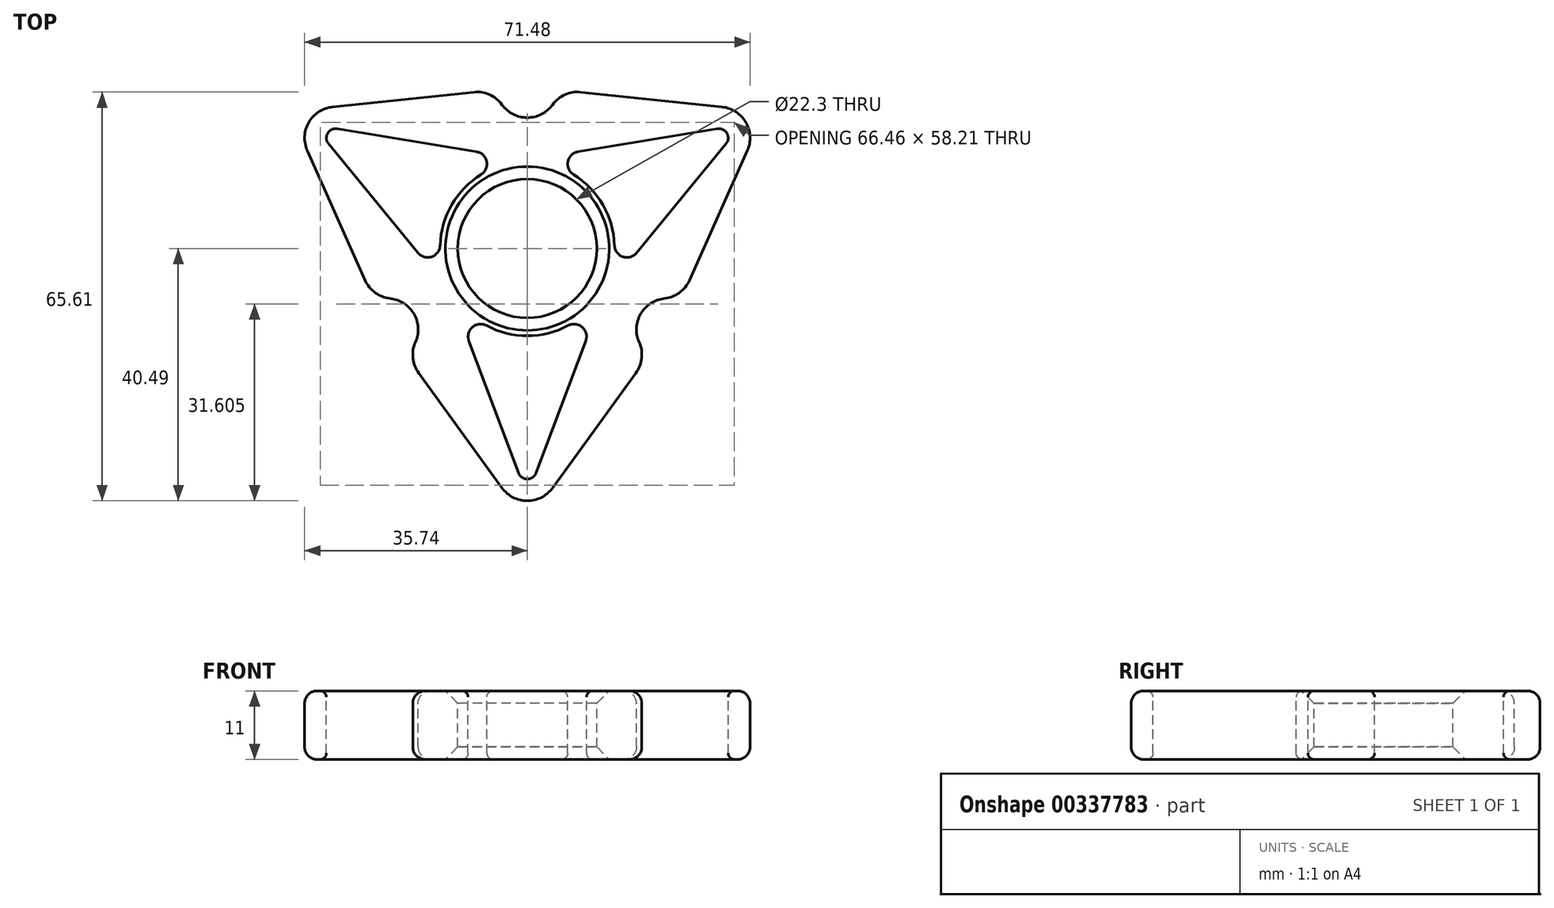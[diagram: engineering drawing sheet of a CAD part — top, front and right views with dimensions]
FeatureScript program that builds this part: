
annotation { "Feature Type Name" : "Feature", "Feature Type Description" : "" }
export const myFeature = defineFeature(function(context is Context, id is Id, definition is map)
    precondition{}
    {
        {
            var Q0;
            Q0=qCreatedBy(makeId("Top.planeOp"),FACE);
            var sketch = newSketch(context, id + "F0", { "sketchPlane" : qUnion([Q0])});
            skCircle(sketch, "E0.cCircle", {"center": v(0, 0) * mm, "radius": 22 * mm, "construction": true});
            skLineSegment(sketch, "E0.0", {"start": v(-38.1, 22) * mm, "end": v(38.1, 22) * mm});
            skLineSegment(sketch, "E0.1", {"start": v(38.1, 22) * mm, "end": v(0, -44) * mm});
            skLineSegment(sketch, "E0.2", {"start": v(0, -44) * mm, "end": v(-38.1, 22) * mm});
            skPoint(sketch, "E0.0.midPoint", {"position": v(0, 22) * mm});
            skLineSegment(sketch, "E1", {"start": v(-38.1, 22) * mm, "end": v(0, 26) * mm});
            skLineSegment(sketch, "E2", {"start": v(0, 26) * mm, "end": v(38.1, 22) * mm});
            skLineSegment(sketch, "E3.1.0", {"start": v(0, -44) * mm, "end": v(-22.52, -13) * mm});
            skLineSegment(sketch, "E3.1.1", {"start": v(-22.52, -13) * mm, "end": v(-38.1, 22) * mm});
            skLineSegment(sketch, "E3.2.0", {"start": v(38.1, 22) * mm, "end": v(22.52, -13) * mm});
            skLineSegment(sketch, "E3.2.1", {"start": v(22.52, -13) * mm, "end": v(0, -44) * mm});
            skSolve(sketch);
        }
        {
            var Q0;
            Q0 = qSketchRegion(id + "F0", true);
            extrude(context, id + "F1", {"entities" : qUnion([Q0]), "depth" : 11 * mm});
        }
        {
            var Q0;
            Q0=makeQuery(id+"F1.opExtrude","CAP_FACE",FACE,{"disambiguationData":[OSD([sQuery(id+"F0.wireOp",EDGE,"E1"),sQuery(id+"F0.wireOp",EDGE,"E2"),sQuery(id+"F0.wireOp",EDGE,"E3.1.0"),sQuery(id+"F0.wireOp",EDGE,"E3.1.1"),sQuery(id+"F0.wireOp",EDGE,"E3.2.0"),sQuery(id+"F0.wireOp",EDGE,"E3.2.1")])],"isStart":false});
            var sketch = newSketch(context, id + "F2", { "sketchPlane" : qUnion([Q0])});
            skCircle(sketch, "E4", {"center": v(0, 0) * mm, "radius": 11.15 * mm});
            skSolve(sketch);
        }
        {
            var Q0;
            Q0 = qSketchRegion(id + "F2", true);
            extrude(context, id + "F3", {"entities" : qUnion([Q0]), "operationType" : NewBodyOperationType.REMOVE, "endBound" : BoundingType.THROUGH_ALL, "oppositeDirection" : true, "depth" : 25 * mm});
        }
        {
            var Q0;
            Q0=makeQuery(id+"F1.opExtrude","SWEPT_EDGE",EDGE,{"disambiguationData":[OSD([sQuery(id+"F0.wireOp",EDGE,"E0.1"),sQuery(id+"F0.wireOp",EDGE,"E0.2"),sQuery(id+"F0.wireOp",EDGE,"E3.1.0"),sQuery(id+"F0.wireOp",EDGE,"E3.2.1")])]});
            var Q1;
            Q1=makeQuery(id+"F1.opExtrude","SWEPT_EDGE",EDGE,{"disambiguationData":[OSD([sQuery(id+"F0.wireOp",EDGE,"E0.0"),sQuery(id+"F0.wireOp",EDGE,"E0.2"),sQuery(id+"F0.wireOp",EDGE,"E1"),sQuery(id+"F0.wireOp",EDGE,"E3.1.1")])]});
            var Q2;
            Q2=makeQuery(id+"F1.opExtrude","SWEPT_EDGE",EDGE,{"disambiguationData":[OSD([sQuery(id+"F0.wireOp",EDGE,"E0.0"),sQuery(id+"F0.wireOp",EDGE,"E0.1"),sQuery(id+"F0.wireOp",EDGE,"E2"),sQuery(id+"F0.wireOp",EDGE,"E3.2.0")])]});
            fillet(context, id + "F4", {"entities" : qUnion([Q0, Q1, Q2]), "radius" : 5 * mm, "tangentPropagation" : true, "allowEdgeOverflow" : false});
        }
        {
            var Q0;
            Q0=makeQuery(id+"F1.opExtrude","CAP_FACE",FACE,{"disambiguationData":[OSD([sQuery(id+"F0.wireOp",EDGE,"E1"),sQuery(id+"F0.wireOp",EDGE,"E2"),sQuery(id+"F0.wireOp",EDGE,"E3.1.0"),sQuery(id+"F0.wireOp",EDGE,"E3.1.1"),sQuery(id+"F0.wireOp",EDGE,"E3.2.0"),sQuery(id+"F0.wireOp",EDGE,"E3.2.1")])],"isStart":false});
            var sketch = newSketch(context, id + "F5", { "sketchPlane" : qUnion([Q0])});
            skArc(sketch, "E5", {"start": v(-4.05, 23.06) * mm, "mid": v(0, 21) * mm, "end": v(4.05, 23.06) * mm});
            skLineSegment(sketch, "E6", {"start": v(-31.26, 22.72) * mm, "end": v(-8.61, 25.1) * mm});
            skLineSegment(sketch, "E7", {"start": v(8.61, 25.1) * mm, "end": v(31.26, 22.72) * mm});
            skPoint(sketch, "E8.visualSharp", {"position": v(-4.97, 25.48) * mm});
            skArc(sketch, "E8.filletArc", {"start": v(-4.05, 23.06) * mm, "mid": v(-6.06, 24.7) * mm, "end": v(-8.61, 25.1) * mm});
            skPoint(sketch, "E9.visualSharp", {"position": v(4.97, 25.48) * mm});
            skArc(sketch, "E9.filletArc", {"start": v(8.61, 25.1) * mm, "mid": v(6.06, 24.7) * mm, "end": v(4.05, 23.06) * mm});
            skLineSegment(sketch, "E10", {"start": v(-8.61, 25.1) * mm, "end": v(0, 26) * mm});
            skLineSegment(sketch, "E11", {"start": v(8.61, 25.1) * mm, "end": v(0, 26) * mm});
            skLineSegment(sketch, "E12.1.0", {"start": v(-4.05, -38.43) * mm, "end": v(-17.43, -20) * mm});
            skLineSegment(sketch, "E12.1.1", {"start": v(-26.04, -5.09) * mm, "end": v(-35.3, 15.71) * mm});
            skPoint(sketch, "E12.1.2", {"position": v(-24.55, -8.43) * mm});
            skLineSegment(sketch, "E12.1.3", {"start": v(-17.43, -20) * mm, "end": v(-22.52, -13) * mm});
            skLineSegment(sketch, "E12.1.4", {"start": v(-26.04, -5.09) * mm, "end": v(-22.52, -13) * mm});
            skPoint(sketch, "E12.1.5", {"position": v(-19.58, -17.05) * mm});
            skArc(sketch, "E12.1.6", {"start": v(-17.95, -15.03) * mm, "mid": v(-18.19, -10.5) * mm, "end": v(-22, -8.03) * mm});
            skArc(sketch, "E12.1.7", {"start": v(-17.95, -15.03) * mm, "mid": v(-18.35, -17.6) * mm, "end": v(-17.43, -20) * mm});
            skArc(sketch, "E12.1.8", {"start": v(-26.04, -5.09) * mm, "mid": v(-24.41, -7.1) * mm, "end": v(-22, -8.03) * mm});
            skLineSegment(sketch, "E12.2.0", {"start": v(35.3, 15.71) * mm, "end": v(26.04, -5.09) * mm});
            skLineSegment(sketch, "E12.2.1", {"start": v(17.43, -20) * mm, "end": v(4.05, -38.43) * mm});
            skPoint(sketch, "E12.2.2", {"position": v(19.58, -17.05) * mm});
            skLineSegment(sketch, "E12.2.3", {"start": v(26.04, -5.09) * mm, "end": v(22.52, -13) * mm});
            skLineSegment(sketch, "E12.2.4", {"start": v(17.43, -20) * mm, "end": v(22.52, -13) * mm});
            skPoint(sketch, "E12.2.5", {"position": v(24.55, -8.43) * mm});
            skArc(sketch, "E12.2.6", {"start": v(22, -8.03) * mm, "mid": v(18.19, -10.5) * mm, "end": v(17.95, -15.03) * mm});
            skArc(sketch, "E12.2.7", {"start": v(22, -8.03) * mm, "mid": v(24.41, -7.1) * mm, "end": v(26.04, -5.09) * mm});
            skArc(sketch, "E12.2.8", {"start": v(17.43, -20) * mm, "mid": v(18.35, -17.6) * mm, "end": v(17.95, -15.03) * mm});
            skPoint(sketch, "E12.center", {"position": v(0, 0) * mm});
            skSolve(sketch);
        }
        {
            var Q0;
            Q0 = qSketchRegion(id + "F5", true);
            extrude(context, id + "F6", {"entities" : qUnion([Q0]), "operationType" : NewBodyOperationType.REMOVE, "endBound" : BoundingType.THROUGH_ALL, "oppositeDirection" : true, "depth" : 25 * mm});
        }
        {
            var Q0;
            Q0=makeQuery(id+"F1.opExtrude","CAP_FACE",FACE,{"disambiguationData":[OSD([sQuery(id+"F0.wireOp",EDGE,"E1"),sQuery(id+"F0.wireOp",EDGE,"E2"),sQuery(id+"F0.wireOp",EDGE,"E3.1.0"),sQuery(id+"F0.wireOp",EDGE,"E3.1.1"),sQuery(id+"F0.wireOp",EDGE,"E3.2.0"),sQuery(id+"F0.wireOp",EDGE,"E3.2.1")])],"isStart":false});
            var sketch = newSketch(context, id + "F7", { "sketchPlane" : qUnion([Q0])});
            skArc(sketch, "E13", {"start": v(-1.4, -36.02) * mm, "mid": v(0, -37) * mm, "end": v(1.4, -36.02) * mm});
            skArc(sketch, "E14", {"start": v(-6.57, -12.36) * mm, "mid": v(0, -14) * mm, "end": v(6.57, -12.36) * mm});
            skLineSegment(sketch, "E15", {"start": v(-9.38, -14.84) * mm, "end": v(-1.4, -36.02) * mm});
            skLineSegment(sketch, "E16", {"start": v(9.38, -14.84) * mm, "end": v(1.4, -36.02) * mm});
            skPoint(sketch, "E17.visualSharp", {"position": v(-13.1, -4.93) * mm});
            skArc(sketch, "E17.filletArc", {"start": v(-6.57, -12.36) * mm, "mid": v(-8.82, -12.63) * mm, "end": v(-9.38, -14.84) * mm});
            skPoint(sketch, "E18.visualSharp", {"position": v(13.1, -4.93) * mm});
            skArc(sketch, "E18.filletArc", {"start": v(9.38, -14.84) * mm, "mid": v(8.82, -12.63) * mm, "end": v(6.57, -12.36) * mm});
            skArc(sketch, "E19.1.0", {"start": v(14, 0.5) * mm, "mid": v(12.12, 7) * mm, "end": v(7.43, 11.87) * mm});
            skArc(sketch, "E19.1.1", {"start": v(8.16, 15.54) * mm, "mid": v(6.53, 13.96) * mm, "end": v(7.43, 11.87) * mm});
            skPoint(sketch, "E19.1.2", {"position": v(10.82, -8.88) * mm});
            skPoint(sketch, "E19.1.3", {"position": v(-2.28, 13.81) * mm});
            skLineSegment(sketch, "E19.1.4", {"start": v(8.16, 15.54) * mm, "end": v(30.5, 19.23) * mm});
            skArc(sketch, "E19.1.5", {"start": v(14, 0.5) * mm, "mid": v(15.35, -1.33) * mm, "end": v(17.54, -0.7) * mm});
            skLineSegment(sketch, "E19.1.6", {"start": v(17.54, -0.7) * mm, "end": v(31.9, 16.8) * mm});
            skArc(sketch, "E19.1.7", {"start": v(31.9, 16.8) * mm, "mid": v(32.04, 18.5) * mm, "end": v(30.5, 19.23) * mm});
            skArc(sketch, "E19.2.0", {"start": v(-7.43, 11.87) * mm, "mid": v(-12.12, 7) * mm, "end": v(-14, 0.5) * mm});
            skArc(sketch, "E19.2.1", {"start": v(-17.54, -0.7) * mm, "mid": v(-15.35, -1.33) * mm, "end": v(-14, 0.5) * mm});
            skPoint(sketch, "E19.2.2", {"position": v(2.28, 13.81) * mm});
            skPoint(sketch, "E19.2.3", {"position": v(-10.82, -8.88) * mm});
            skLineSegment(sketch, "E19.2.4", {"start": v(-17.54, -0.7) * mm, "end": v(-31.9, 16.8) * mm});
            skArc(sketch, "E19.2.5", {"start": v(-7.43, 11.87) * mm, "mid": v(-6.53, 13.96) * mm, "end": v(-8.16, 15.54) * mm});
            skLineSegment(sketch, "E19.2.6", {"start": v(-8.16, 15.54) * mm, "end": v(-30.5, 19.23) * mm});
            skArc(sketch, "E19.2.7", {"start": v(-30.5, 19.23) * mm, "mid": v(-32.04, 18.5) * mm, "end": v(-31.9, 16.8) * mm});
            skSolve(sketch);
        }
        {
            var Q0;
            Q0=makeQuery(id+"F4.opFillet","BLEND_FACE",FACE,{"disambiguationData":[OSD([sQuery(id+"F0.wireOp",EDGE,"E0.0"),sQuery(id+"F0.wireOp",EDGE,"E0.2"),sQuery(id+"F0.wireOp",EDGE,"E1"),sQuery(id+"F0.wireOp",EDGE,"E3.1.1")])]});
            var Q1;
            Q1=makeQuery(id+"F1.opExtrude","SWEPT_FACE",FACE,{"disambiguationData":[OSD([sQuery(id+"F0.wireOp",EDGE,"E3.1.1")])]});
            var Q2;
            Q2=makeQuery(id+"F6.boolean.opBoolean","COPY",FACE,{"derivedFrom":makeQuery(id+"F6.opExtrude","SWEPT_FACE",FACE,{"disambiguationData":[OSD([sQuery(id+"F5.wireOp",EDGE,"E12.1.8")])]})});
            var Q3;
            Q3=makeQuery(id+"F6.boolean.opBoolean","COPY",FACE,{"derivedFrom":makeQuery(id+"F6.opExtrude","SWEPT_FACE",FACE,{"disambiguationData":[OSD([sQuery(id+"F5.wireOp",EDGE,"E12.1.6")])]})});
            var Q4;
            Q4=makeQuery(id+"F6.boolean.opBoolean","COPY",FACE,{"derivedFrom":makeQuery(id+"F6.opExtrude","SWEPT_FACE",FACE,{"disambiguationData":[OSD([sQuery(id+"F5.wireOp",EDGE,"E12.1.7")])]})});
            var Q5;
            Q5=makeQuery(id+"F1.opExtrude","SWEPT_FACE",FACE,{"disambiguationData":[OSD([sQuery(id+"F0.wireOp",EDGE,"E3.1.0")])]});
            var Q6;
            Q6=makeQuery(id+"F4.opFillet","BLEND_FACE",FACE,{"disambiguationData":[OSD([sQuery(id+"F0.wireOp",EDGE,"E0.1"),sQuery(id+"F0.wireOp",EDGE,"E0.2"),sQuery(id+"F0.wireOp",EDGE,"E3.1.0"),sQuery(id+"F0.wireOp",EDGE,"E3.2.1")])]});
            var Q7;
            Q7=makeQuery(id+"F1.opExtrude","SWEPT_FACE",FACE,{"disambiguationData":[OSD([sQuery(id+"F0.wireOp",EDGE,"E3.2.1")])]});
            var Q8;
            Q8=makeQuery(id+"F6.boolean.opBoolean","COPY",FACE,{"derivedFrom":makeQuery(id+"F6.opExtrude","SWEPT_FACE",FACE,{"disambiguationData":[OSD([sQuery(id+"F5.wireOp",EDGE,"E12.2.8")])]})});
            var Q9;
            Q9=makeQuery(id+"F6.boolean.opBoolean","COPY",FACE,{"derivedFrom":makeQuery(id+"F6.opExtrude","SWEPT_FACE",FACE,{"disambiguationData":[OSD([sQuery(id+"F5.wireOp",EDGE,"E12.2.6")])]})});
            var Q10;
            Q10=makeQuery(id+"F6.boolean.opBoolean","COPY",FACE,{"derivedFrom":makeQuery(id+"F6.opExtrude","SWEPT_FACE",FACE,{"disambiguationData":[OSD([sQuery(id+"F5.wireOp",EDGE,"E12.2.7")])]})});
            var Q11;
            Q11=makeQuery(id+"F1.opExtrude","SWEPT_FACE",FACE,{"disambiguationData":[OSD([sQuery(id+"F0.wireOp",EDGE,"E3.2.0")])]});
            var Q12;
            Q12=makeQuery(id+"F4.opFillet","BLEND_FACE",FACE,{"disambiguationData":[OSD([sQuery(id+"F0.wireOp",EDGE,"E0.0"),sQuery(id+"F0.wireOp",EDGE,"E0.1"),sQuery(id+"F0.wireOp",EDGE,"E2"),sQuery(id+"F0.wireOp",EDGE,"E3.2.0")])]});
            var Q13;
            Q13=makeQuery(id+"F1.opExtrude","SWEPT_FACE",FACE,{"disambiguationData":[OSD([sQuery(id+"F0.wireOp",EDGE,"E2")])]});
            var Q14;
            Q14=makeQuery(id+"F6.boolean.opBoolean","COPY",FACE,{"derivedFrom":makeQuery(id+"F6.opExtrude","SWEPT_FACE",FACE,{"disambiguationData":[OSD([sQuery(id+"F5.wireOp",EDGE,"E9.filletArc")])]})});
            var Q15;
            Q15=makeQuery(id+"F6.boolean.opBoolean","COPY",FACE,{"derivedFrom":makeQuery(id+"F6.opExtrude","SWEPT_FACE",FACE,{"disambiguationData":[OSD([sQuery(id+"F5.wireOp",EDGE,"E5")])]})});
            var Q16;
            Q16=makeQuery(id+"F6.boolean.opBoolean","COPY",FACE,{"derivedFrom":makeQuery(id+"F6.opExtrude","SWEPT_FACE",FACE,{"disambiguationData":[OSD([sQuery(id+"F5.wireOp",EDGE,"E8.filletArc")])]})});
            var Q17;
            Q17=makeQuery(id+"F1.opExtrude","SWEPT_FACE",FACE,{"disambiguationData":[OSD([sQuery(id+"F0.wireOp",EDGE,"E1")])]});
            fillet(context, id + "F8", {"entities" : qUnion([Q0, Q1, Q2, Q3, Q4, Q5, Q6, Q7, Q8, Q9, Q10, Q11, Q12, Q13, Q14, Q15, Q16, Q17]), "radius" : 2 * mm, "tangentPropagation" : true, "allowEdgeOverflow" : false});
        }
        {
            var Q0;
            Q0 = qSketchRegion(id + "F7", true);
            extrude(context, id + "F9", {"entities" : qUnion([Q0]), "operationType" : NewBodyOperationType.REMOVE, "endBound" : BoundingType.THROUGH_ALL, "oppositeDirection" : true, "depth" : 25 * mm});
        }
        {
            var Q0;
            Q0=makeQuery(id+"F9.boolean.opBoolean","COPY",FACE,{"derivedFrom":makeQuery(id+"F9.opExtrude","SWEPT_FACE",FACE,{"disambiguationData":[OSD([sQuery(id+"F7.wireOp",EDGE,"E19.1.7")])]})});
            var Q1;
            Q1=makeQuery(id+"F9.boolean.opBoolean","COPY",FACE,{"derivedFrom":makeQuery(id+"F9.opExtrude","SWEPT_FACE",FACE,{"disambiguationData":[OSD([sQuery(id+"F7.wireOp",EDGE,"E19.1.4")])]})});
            var Q2;
            Q2=makeQuery(id+"F9.boolean.opBoolean","COPY",FACE,{"derivedFrom":makeQuery(id+"F9.opExtrude","SWEPT_FACE",FACE,{"disambiguationData":[OSD([sQuery(id+"F7.wireOp",EDGE,"E19.2.6")])]})});
            var Q3;
            Q3=makeQuery(id+"F9.boolean.opBoolean","COPY",FACE,{"derivedFrom":makeQuery(id+"F9.opExtrude","SWEPT_FACE",FACE,{"disambiguationData":[OSD([sQuery(id+"F7.wireOp",EDGE,"E19.2.5")])]})});
            var Q4;
            Q4=makeQuery(id+"F9.boolean.opBoolean","COPY",FACE,{"derivedFrom":makeQuery(id+"F9.opExtrude","SWEPT_FACE",FACE,{"disambiguationData":[OSD([sQuery(id+"F7.wireOp",EDGE,"E19.2.0")])]})});
            var Q5;
            Q5=makeQuery(id+"F9.boolean.opBoolean","COPY",FACE,{"derivedFrom":makeQuery(id+"F9.opExtrude","SWEPT_FACE",FACE,{"disambiguationData":[OSD([sQuery(id+"F7.wireOp",EDGE,"E19.1.6")])]})});
            var Q6;
            Q6=makeQuery(id+"F9.boolean.opBoolean","COPY",FACE,{"derivedFrom":makeQuery(id+"F9.opExtrude","SWEPT_FACE",FACE,{"disambiguationData":[OSD([sQuery(id+"F7.wireOp",EDGE,"E14")])]})});
            var Q7;
            Q7=makeQuery(id+"F9.boolean.opBoolean","COPY",FACE,{"derivedFrom":makeQuery(id+"F9.opExtrude","SWEPT_FACE",FACE,{"disambiguationData":[OSD([sQuery(id+"F7.wireOp",EDGE,"E18.filletArc")])]})});
            var Q8;
            Q8=makeQuery(id+"F9.boolean.opBoolean","COPY",FACE,{"derivedFrom":makeQuery(id+"F9.opExtrude","SWEPT_FACE",FACE,{"disambiguationData":[OSD([sQuery(id+"F7.wireOp",EDGE,"E16")])]})});
            var Q9;
            Q9=makeQuery(id+"F9.boolean.opBoolean","COPY",FACE,{"derivedFrom":makeQuery(id+"F9.opExtrude","SWEPT_FACE",FACE,{"disambiguationData":[OSD([sQuery(id+"F7.wireOp",EDGE,"E19.2.4")])]})});
            var Q10;
            Q10=makeQuery(id+"F9.boolean.opBoolean","COPY",FACE,{"derivedFrom":makeQuery(id+"F9.opExtrude","SWEPT_FACE",FACE,{"disambiguationData":[OSD([sQuery(id+"F7.wireOp",EDGE,"E19.1.0")])]})});
            var Q11;
            Q11=makeQuery(id+"F9.boolean.opBoolean","COPY",FACE,{"derivedFrom":makeQuery(id+"F9.opExtrude","SWEPT_FACE",FACE,{"disambiguationData":[OSD([sQuery(id+"F7.wireOp",EDGE,"E19.1.1")])]})});
            var Q12;
            Q12=makeQuery(id+"F9.boolean.opBoolean","COPY",FACE,{"derivedFrom":makeQuery(id+"F9.opExtrude","SWEPT_FACE",FACE,{"disambiguationData":[OSD([sQuery(id+"F7.wireOp",EDGE,"E15")])]})});
            var Q13;
            Q13=makeQuery(id+"F9.boolean.opBoolean","COPY",FACE,{"derivedFrom":makeQuery(id+"F9.opExtrude","SWEPT_FACE",FACE,{"disambiguationData":[OSD([sQuery(id+"F7.wireOp",EDGE,"E19.2.7")])]})});
            var Q14;
            Q14=makeQuery(id+"F9.boolean.opBoolean","COPY",FACE,{"derivedFrom":makeQuery(id+"F9.opExtrude","SWEPT_FACE",FACE,{"disambiguationData":[OSD([sQuery(id+"F7.wireOp",EDGE,"E17.filletArc")])]})});
            var Q15;
            Q15=makeQuery(id+"F9.boolean.opBoolean","COPY",FACE,{"derivedFrom":makeQuery(id+"F9.opExtrude","SWEPT_FACE",FACE,{"disambiguationData":[OSD([sQuery(id+"F7.wireOp",EDGE,"E19.2.1")])]})});
            var Q16;
            Q16=makeQuery(id+"F9.boolean.opBoolean","COPY",FACE,{"derivedFrom":makeQuery(id+"F9.opExtrude","SWEPT_FACE",FACE,{"disambiguationData":[OSD([sQuery(id+"F7.wireOp",EDGE,"E19.1.5")])]})});
            var Q17;
            Q17=makeQuery(id+"F9.boolean.opBoolean","COPY",FACE,{"derivedFrom":makeQuery(id+"F9.opExtrude","SWEPT_FACE",FACE,{"disambiguationData":[OSD([sQuery(id+"F7.wireOp",EDGE,"E13")])]})});
            fillet(context, id + "F10", {"entities" : qUnion([Q0, Q1, Q2, Q3, Q4, Q5, Q6, Q7, Q8, Q9, Q10, Q11, Q12, Q13, Q14, Q15, Q16, Q17]), "radius" : 1 * mm, "tangentPropagation" : true, "allowEdgeOverflow" : false});
        }
        {
            var Q0;
            Q0=makeQuery(id+"F3.boolean.opBoolean","COPY",FACE,{"derivedFrom":makeQuery(id+"F3.opExtrude","SWEPT_FACE",FACE,{"disambiguationData":[OSD([sQuery(id+"F2.wireOp",EDGE,"E4")])]})});
            chamfer(context, id + "F11", {"entities" : qUnion([Q0]), "width" : 2 * mm, "tangentPropagation" : true});
        }
    });
